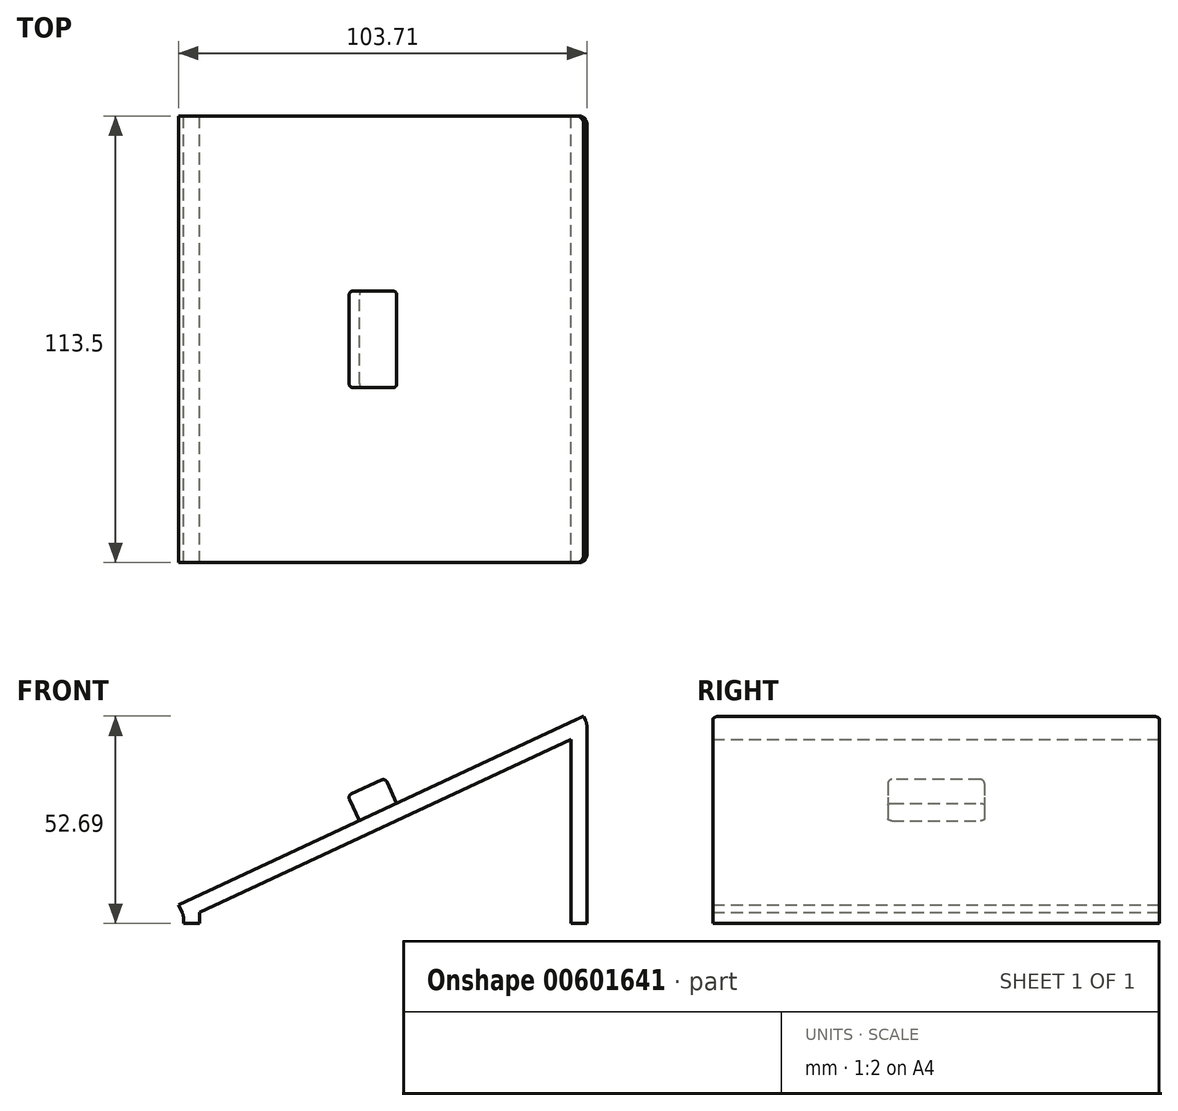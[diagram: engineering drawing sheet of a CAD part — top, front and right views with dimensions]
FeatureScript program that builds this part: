
annotation { "Feature Type Name" : "Feature", "Feature Type Description" : "" }
export const myFeature = defineFeature(function(context is Context, id is Id, definition is map)
    precondition{}
    {
        {
            var Q0;
            Q0=qCreatedBy(makeId("Front.planeOp"),FACE);
            var sketch = newSketch(context, id + "F0", { "sketchPlane" : qUnion([Q0])});
            skLineSegment(sketch, "E0", {"start": v(-51.22, 0) * mm, "end": v(51.22, 0) * mm, "construction": true});
            skLineSegment(sketch, "E1", {"start": v(51.22, 0) * mm, "end": v(51.22, 50.87) * mm});
            skLineSegment(sketch, "E2", {"start": v(-51.22, 2) * mm, "end": v(-51.22, 0) * mm});
            skLineSegment(sketch, "E3", {"start": v(-51.22, 2) * mm, "end": v(-52.49, 4.72) * mm});
            skLineSegment(sketch, "E4", {"start": v(51.22, 50.87) * mm, "end": v(50.38, 52.69) * mm});
            skLineSegment(sketch, "E5", {"start": v(-52.49, 4.72) * mm, "end": v(50.38, 52.69) * mm});
            skLineSegment(sketch, "E6.0", {"start": v(47.22, 0) * mm, "end": v(47.22, 46.8) * mm});
            skLineSegment(sketch, "E6.1", {"start": v(-47.17, 2.78) * mm, "end": v(47.22, 46.8) * mm});
            skLineSegment(sketch, "E6.2", {"start": v(-47.17, 2.78) * mm, "end": v(-47.22, 2.89) * mm});
            skLineSegment(sketch, "E6.3", {"start": v(-47.22, 2.89) * mm, "end": v(-47.22, 0) * mm});
            skLineSegment(sketch, "E7", {"start": v(-51.22, 0) * mm, "end": v(-47.22, 0) * mm});
            skLineSegment(sketch, "E8", {"start": v(47.22, 0) * mm, "end": v(51.22, 0) * mm});
            skSolve(sketch);
        }
        {
            var Q0;
            Q0=makeQuery(id+"F0.imprint","IMPRINT",FACE,{"disambiguationData":[TD([[makeQuery(id+"F0.imprint","IMPRINT",EDGE,{"derivedFrom":sQuery(id+"F0.wireOp",EDGE,"E1")}),1.0]])]});
            extrude(context, id + "F1", {"entities" : qUnion([Q0]), "endBound" : BoundingType.SYMMETRIC, "depth" : 113.5 * mm});
        }
        {
            var Q0;
            Q0=makeQuery(id+"F1.opExtrude","SWEPT_EDGE",EDGE,{"disambiguationData":[OSD([sQuery(id+"F0.wireOp",EDGE,"E1"),sQuery(id+"F0.wireOp",EDGE,"E4")])]});
            var Q1;
            Q1=makeQuery(id+"F1.opExtrude","SWEPT_EDGE",EDGE,{"disambiguationData":[OSD([sQuery(id+"F0.wireOp",EDGE,"E2"),sQuery(id+"F0.wireOp",EDGE,"E3")])]});
            fillet(context, id + "F2", {"entities" : qUnion([Q0, Q1]), "radius" : 4 * mm, "tangentPropagation" : true, "allowEdgeOverflow" : false});
        }
        {
            var Q0;
            Q0=makeQuery(id+"F1.opExtrude","SWEPT_FACE",FACE,{"disambiguationData":[OSD([sQuery(id+"F0.wireOp",EDGE,"E5")])]});
            var sketch = newSketch(context, id + "F3", { "sketchPlane" : qUnion([Q0])});
            skLineSegment(sketch, "E9", {"start": v(-46.42, 0) * mm, "end": v(67.08, 0) * mm, "construction": true});
            skPoint(sketch, "E10", {"position": v(10.33, 0) * mm});
            skLineSegment(sketch, "E11", {"start": v(10.33, 44.71) * mm, "end": v(10.33, -42.62) * mm, "construction": true});
            skLineSegment(sketch, "E12.bottom", {"start": v(14.58, -12.25) * mm, "end": v(6.08, -12.25) * mm});
            skLineSegment(sketch, "E12.top", {"start": v(14.58, 12.25) * mm, "end": v(6.08, 12.25) * mm});
            skLineSegment(sketch, "E12.left", {"start": v(15.58, -11.25) * mm, "end": v(15.58, 11.25) * mm});
            skLineSegment(sketch, "E12.right", {"start": v(5.08, -11.25) * mm, "end": v(5.08, 11.25) * mm});
            skPoint(sketch, "E13.visualSharp", {"position": v(5.08, 12.25) * mm});
            skArc(sketch, "E13.filletArc", {"start": v(6.08, 12.25) * mm, "mid": v(5.37, 11.96) * mm, "end": v(5.08, 11.25) * mm});
            skPoint(sketch, "E14.visualSharp", {"position": v(15.58, 12.25) * mm});
            skArc(sketch, "E14.filletArc", {"start": v(15.58, 11.25) * mm, "mid": v(15.28, 11.96) * mm, "end": v(14.58, 12.25) * mm});
            skPoint(sketch, "E15.visualSharp", {"position": v(15.58, -12.25) * mm});
            skArc(sketch, "E15.filletArc", {"start": v(14.58, -12.25) * mm, "mid": v(15.28, -11.96) * mm, "end": v(15.58, -11.25) * mm});
            skPoint(sketch, "E16.visualSharp", {"position": v(5.08, -12.25) * mm});
            skArc(sketch, "E16.filletArc", {"start": v(5.08, -11.25) * mm, "mid": v(5.37, -11.96) * mm, "end": v(6.08, -12.25) * mm});
            skSolve(sketch);
        }
        {
            var Q0;
            Q0=makeQuery(id+"F3.imprint","IMPRINT",FACE,{"disambiguationData":[TD([[makeQuery(id+"F3.imprint","IMPRINT",EDGE,{"derivedFrom":sQuery(id+"F3.wireOp",EDGE,"E12.bottom")}),-1.0]])]});
            extrude(context, id + "F4", {"entities" : qUnion([Q0]), "operationType" : NewBodyOperationType.ADD, "depth" : 7 * mm});
        }
        {
            var Q0;
            Q0=makeQuery(id+"F4.opExtrude","CAP_EDGE",EDGE,{"disambiguationData":[OSD([sQuery(id+"F3.wireOp",EDGE,"E12.bottom")])],"isStart":false});
            fillet(context, id + "F5", {"entities" : qUnion([Q0]), "radius" : 1 * mm, "tangentPropagation" : true, "allowEdgeOverflow" : false});
        }
        {
            var Q0;
            Q0=makeQuery(id+"F1.opExtrude","CAP_EDGE",EDGE,{"disambiguationData":[OSD([sQuery(id+"F0.wireOp",EDGE,"E1")])],"isStart":false});
            var Q1;
            Q1=makeQuery(id+"F1.opExtrude","CAP_EDGE",EDGE,{"disambiguationData":[OSD([sQuery(id+"F0.wireOp",EDGE,"E1")])],"isStart":true});
            fillet(context, id + "F6", {"entities" : qUnion([Q0, Q1]), "radius" : 2 * mm, "tangentPropagation" : true, "allowEdgeOverflow" : false});
        }
    });
